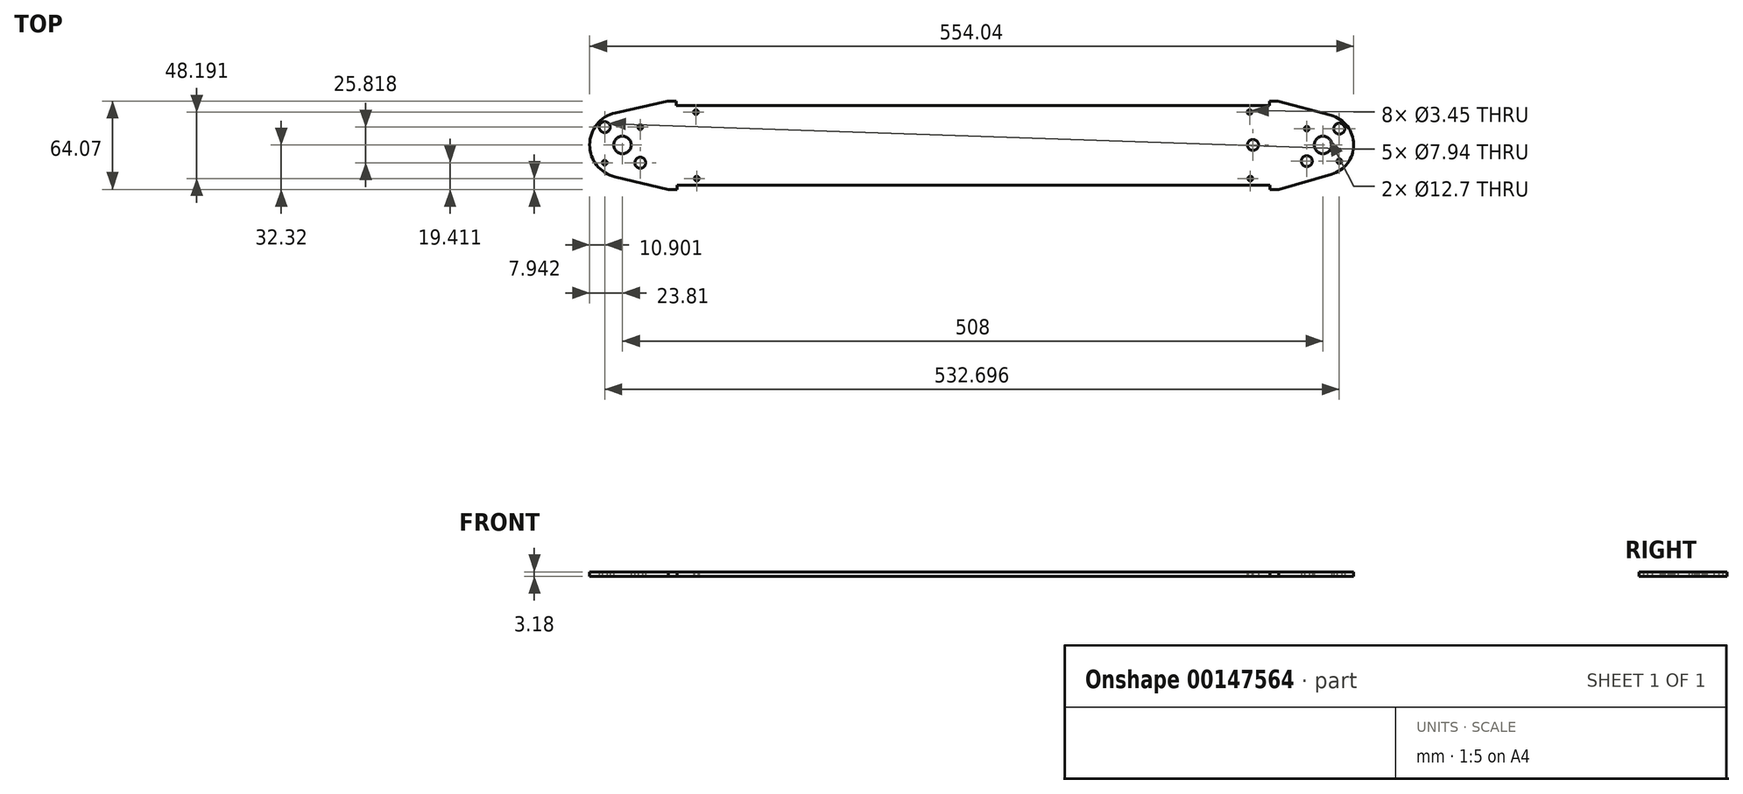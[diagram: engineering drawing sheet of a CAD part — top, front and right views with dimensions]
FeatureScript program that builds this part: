
annotation { "Feature Type Name" : "Feature", "Feature Type Description" : "" }
export const myFeature = defineFeature(function(context is Context, id is Id, definition is map)
    precondition{}
    {
        {
            var Q0;
            Q0=qCreatedBy(makeId("Top.planeOp"),FACE);
            var sketch = newSketch(context, id + "F0", { "sketchPlane" : qUnion([Q0])});
            skPoint(sketch, "E0.rect.middle", {"position": v(0, 0) * mm});
            skCircle(sketch, "E1", {"center": v(0, 0) * mm, "radius": 11.11 * mm, "construction": true});
            skLineSegment(sketch, "E2.bottom", {"start": v(11.79, 11.79) * mm, "end": v(-11.79, 11.79) * mm, "construction": true});
            skLineSegment(sketch, "E2.left", {"start": v(11.79, 11.79) * mm, "end": v(11.79, -11.79) * mm, "construction": true});
            skLineSegment(sketch, "E2.right", {"start": v(-11.79, 11.79) * mm, "end": v(-11.79, -11.79) * mm, "construction": true});
            skCircle(sketch, "E3", {"center": v(11.79, 11.79) * mm, "radius": 5.56 * mm, "construction": true});
            skCircle(sketch, "E4", {"center": v(-11.79, 11.79) * mm, "radius": 1.73 * mm});
            skCircle(sketch, "E5", {"center": v(11.79, 11.79) * mm, "radius": 3.97 * mm});
            skCircle(sketch, "E6", {"center": v(11.79, -11.79) * mm, "radius": 1.73 * mm});
            skCircle(sketch, "E7", {"center": v(-11.79, -11.79) * mm, "radius": 3.97 * mm});
            skArc(sketch, "E8", {"start": v(-513.23, 23.23) * mm, "mid": v(-531.81, 0.13) * mm, "end": v(-513.48, -23.17) * mm});
            skLineSegment(sketch, "E9.bottom", {"start": v(-520.9, 12.9) * mm, "end": v(-495.1, 12.9) * mm, "construction": true});
            skLineSegment(sketch, "E9.top", {"start": v(-520.9, -12.9) * mm, "end": v(-495.1, -12.9) * mm, "construction": true});
            skLineSegment(sketch, "E9.left", {"start": v(-520.9, 12.9) * mm, "end": v(-520.9, -12.9) * mm, "construction": true});
            skLineSegment(sketch, "E9.right", {"start": v(-495.1, 12.9) * mm, "end": v(-495.1, -12.9) * mm, "construction": true});
            skCircle(sketch, "E10", {"center": v(-495.1, 12.9) * mm, "radius": 1.73 * mm});
            skCircle(sketch, "E11", {"center": v(-508, 0) * mm, "radius": 6.35 * mm});
            skCircle(sketch, "E12", {"center": v(-520.9, 12.9) * mm, "radius": 3.97 * mm});
            skCircle(sketch, "E13", {"center": v(-520.9, -12.9) * mm, "radius": 1.73 * mm});
            skCircle(sketch, "E14", {"center": v(-495.1, -12.9) * mm, "radius": 3.97 * mm});
            skLineSegment(sketch, "E15", {"start": v(0, 0) * mm, "end": v(-508, 0) * mm, "construction": true});
            skLineSegment(sketch, "E16", {"start": v(-513.48, -23.17) * mm, "end": v(-474.82, -32.32) * mm});
            skLineSegment(sketch, "E17", {"start": v(-513.23, 23.23) * mm, "end": v(-475.38, 31.75) * mm});
            skLineSegment(sketch, "E18", {"start": v(-468.47, -29.14) * mm, "end": v(-38.41, -29.14) * mm});
            skLineSegment(sketch, "E19", {"start": v(-469.03, 28.57) * mm, "end": v(-38.97, 28.57) * mm});
            skLineSegment(sketch, "E20", {"start": v(-469.03, 31.75) * mm, "end": v(-469.03, 28.57) * mm});
            skLineSegment(sketch, "E21", {"start": v(-469.03, 31.75) * mm, "end": v(-475.38, 31.75) * mm});
            skLineSegment(sketch, "E22", {"start": v(-468.47, -29.14) * mm, "end": v(-468.47, -32.32) * mm});
            skLineSegment(sketch, "E23", {"start": v(-468.47, -32.32) * mm, "end": v(-474.82, -32.32) * mm});
            skLineSegment(sketch, "E24", {"start": v(-38.41, -29.14) * mm, "end": v(-38.41, -32.32) * mm});
            skLineSegment(sketch, "E25", {"start": v(-38.41, -32.32) * mm, "end": v(-32.06, -32.32) * mm});
            skLineSegment(sketch, "E26", {"start": v(-38.97, 28.57) * mm, "end": v(-38.97, 31.75) * mm});
            skLineSegment(sketch, "E27", {"start": v(-38.97, 31.75) * mm, "end": v(-32.62, 31.75) * mm});
            skLineSegment(sketch, "E28", {"start": v(-32.06, -32.32) * mm, "end": v(6.13, -21.36) * mm});
            skLineSegment(sketch, "E29", {"start": v(5.75, 21.47) * mm, "end": v(-32.62, 31.75) * mm});
            skArc(sketch, "E30", {"start": v(6.13, -21.36) * mm, "mid": v(22.22, 0.2) * mm, "end": v(5.75, 21.47) * mm});
            skLineSegment(sketch, "E31", {"start": v(-469.03, 28.57) * mm, "end": v(-469.03, 23.81) * mm, "construction": true});
            skLineSegment(sketch, "E32", {"start": v(-469.03, 23.81) * mm, "end": v(-454.74, 23.81) * mm, "construction": true});
            skLineSegment(sketch, "E33", {"start": v(-468.47, -29.14) * mm, "end": v(-468.47, -24.38) * mm, "construction": true});
            skLineSegment(sketch, "E34", {"start": v(-468.47, -24.38) * mm, "end": v(-454.18, -24.38) * mm, "construction": true});
            skLineSegment(sketch, "E35", {"start": v(-38.41, -29.14) * mm, "end": v(-38.41, -24.38) * mm, "construction": true});
            skLineSegment(sketch, "E36", {"start": v(-38.41, -24.38) * mm, "end": v(-52.7, -24.38) * mm, "construction": true});
            skLineSegment(sketch, "E37", {"start": v(-38.97, 28.57) * mm, "end": v(-38.97, 23.81) * mm, "construction": true});
            skLineSegment(sketch, "E38", {"start": v(-38.97, 23.81) * mm, "end": v(-53.26, 23.81) * mm, "construction": true});
            skCircle(sketch, "E39", {"center": v(-454.74, 23.81) * mm, "radius": 1.73 * mm});
            skCircle(sketch, "E40", {"center": v(-53.26, 23.81) * mm, "radius": 1.73 * mm});
            skCircle(sketch, "E41", {"center": v(-52.7, -24.38) * mm, "radius": 1.73 * mm});
            skCircle(sketch, "E42", {"center": v(-454.18, -24.38) * mm, "radius": 1.73 * mm});
            skLineSegment(sketch, "E43", {"start": v(-11.79, -11.79) * mm, "end": v(11.79, -11.79) * mm, "construction": true});
            skLineSegment(sketch, "E44", {"start": v(-254, -28.58) * mm, "end": v(-254, 0) * mm, "construction": true});
            skLineSegment(sketch, "E45", {"start": v(-254, 0) * mm, "end": v(-254, 28.58) * mm, "construction": true});
            skLineSegment(sketch, "E46", {"start": v(-11.79, 11.79) * mm, "end": v(-50.8, 11.79) * mm, "construction": true});
            skLineSegment(sketch, "E47", {"start": v(-50.8, 11.79) * mm, "end": v(-50.8, 0) * mm, "construction": true});
            skCircle(sketch, "E48", {"center": v(-50.8, 0) * mm, "radius": 3.97 * mm});
            skCircle(sketch, "E49", {"center": v(-520.9, -12.9) * mm, "radius": 5.56 * mm, "construction": true});
            skCircle(sketch, "E50", {"center": v(0, 0) * mm, "radius": 6.35 * mm});
            skSolve(sketch);
        }
        {
            var Q0;
            Q0=qSketchRegion(id+"F0",true);
            extrude(context, id + "F1", {"entities" : qUnion([Q0]), "depth" : 3.17 * mm});
        }
    });
